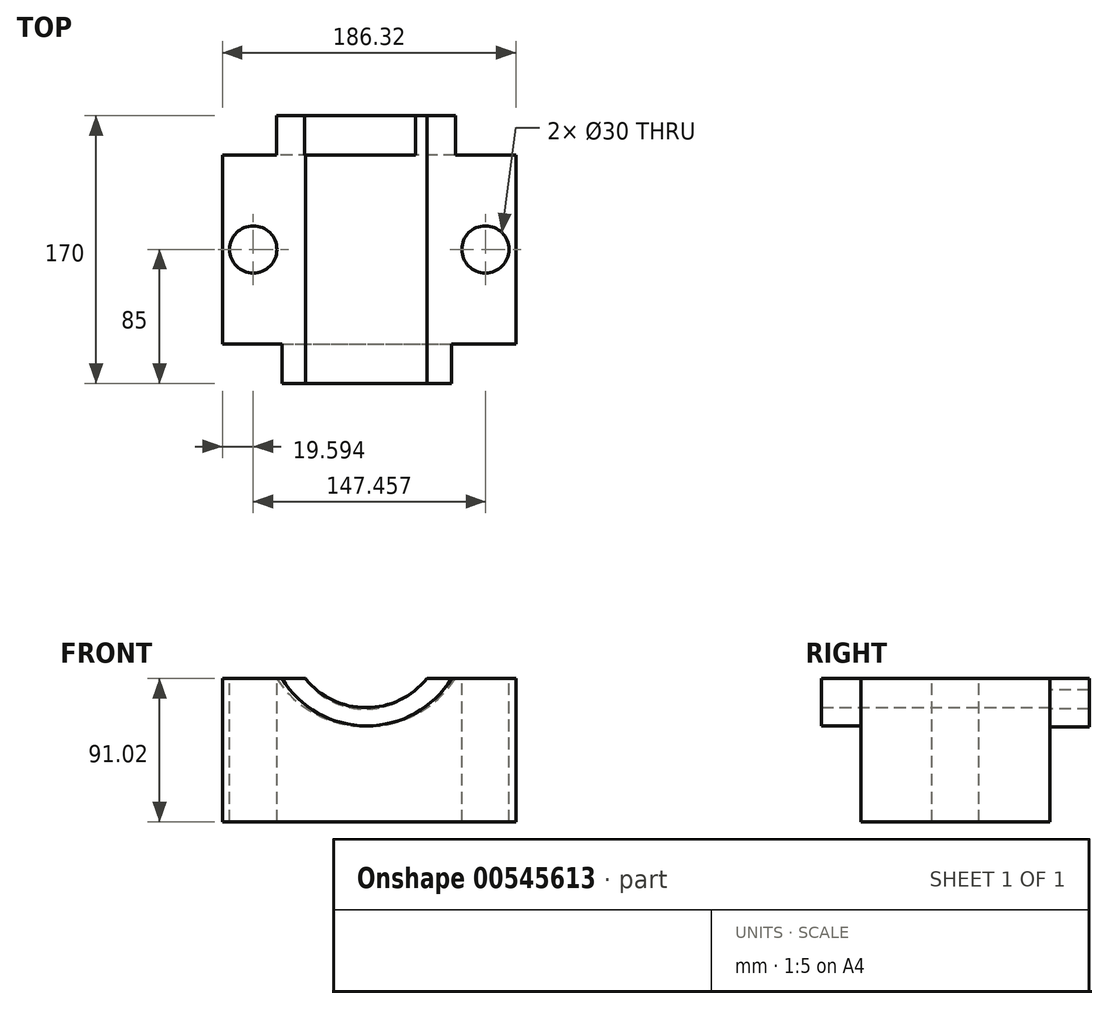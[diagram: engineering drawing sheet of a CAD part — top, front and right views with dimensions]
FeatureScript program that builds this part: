
annotation { "Feature Type Name" : "Feature", "Feature Type Description" : "" }
export const myFeature = defineFeature(function(context is Context, id is Id, definition is map)
    precondition{}
    {
        {
            var Q0;
            Q0=qCreatedBy(makeId("Front.planeOp"),FACE);
            var sketch = newSketch(context, id + "F0", { "sketchPlane" : qUnion([Q0])});
            skLineSegment(sketch, "E0.bottom", {"start": v(-92.59, 41.23) * mm, "end": v(93.73, 41.23) * mm});
            skLineSegment(sketch, "E0.top", {"start": v(-92.59, -49.79) * mm, "end": v(93.73, -49.79) * mm});
            skLineSegment(sketch, "E0.left", {"start": v(-92.59, 41.23) * mm, "end": v(-92.59, -49.79) * mm});
            skLineSegment(sketch, "E0.right", {"start": v(93.73, 41.23) * mm, "end": v(93.73, -49.79) * mm});
            skSolve(sketch);
        }
        {
            var Q0;
            Q0=makeQuery(id+"F0.imprint","IMPRINT",FACE,{"disambiguationData":[TD([[makeQuery(id+"F0.imprint","IMPRINT",EDGE,{"derivedFrom":sQuery(id+"F0.wireOp",EDGE,"E0.bottom")}),-1.0]])]});
            extrude(context, id + "F1", {"entities" : qUnion([Q0]), "depth" : 120 * mm, "offsetDistance" : 25 * mm, "symmetric" : true});
        }
        {
            var Q0;
            Q0=makeQuery(id+"F1.opExtrude","CAP_FACE",FACE,{"disambiguationData":[OSD([sQuery(id+"F0.wireOp",EDGE,"E0.bottom"),sQuery(id+"F0.wireOp",EDGE,"E0.top"),sQuery(id+"F0.wireOp",EDGE,"E0.left"),sQuery(id+"F0.wireOp",EDGE,"E0.right")])],"isStart":false});
            var sketch = newSketch(context, id + "F2", { "sketchPlane" : qUnion([Q0])});
            skArc(sketch, "E1", {"start": v(-40.37, 41.8) * mm, "mid": v(-1.7, 22.73) * mm, "end": v(37.24, 41.23) * mm});
            skArc(sketch, "E2", {"start": v(-55.21, 41.8) * mm, "mid": v(-1, 11.12) * mm, "end": v(53.21, 41.8) * mm});
            skSolve(sketch);
        }
        {
            var Q0;
            {var subQ0=sQuery(id+"F2.wireOp",EDGE,"E1");var subQ1=makeQuery(id+"F1.opExtrude","CAP_EDGE",EDGE,{"disambiguationData":[OSD([sQuery(id+"F0.wireOp",EDGE,"E0.bottom")])],"isStart":false});var subQ2=makeQuery(id+"F2.imprint","INTERSECT",VERTEX,{"disambiguationData":[OD(0.0)],"derivedFrom":[subQ1,subQ0]});Q0=makeQuery(id+"F2.imprint","IMPRINT",FACE,{"disambiguationData":[TD([[makeQuery(id+"F2.imprint","IMPRINT",EDGE,{"disambiguationData":[TD([[subQ2,1.0]])],"derivedFrom":subQ0}),-1.0]])]});}
            extrude(context, id + "F3", {"entities" : qUnion([Q0]), "operationType" : NewBodyOperationType.ADD, "depth" : 25 * mm, "offsetDistance" : 25 * mm});
        }
        {
            var Q0;
            Q0=makeQuery(id+"F1.opExtrude","CAP_FACE",FACE,{"disambiguationData":[OSD([sQuery(id+"F0.wireOp",EDGE,"E0.bottom"),sQuery(id+"F0.wireOp",EDGE,"E0.top"),sQuery(id+"F0.wireOp",EDGE,"E0.left"),sQuery(id+"F0.wireOp",EDGE,"E0.right")])],"isStart":true});
            var sketch = newSketch(context, id + "F4", { "sketchPlane" : qUnion([Q0])});
            skArc(sketch, "E3", {"start": v(-55.4, 41.23) * mm, "mid": v(1.44, 10.6) * mm, "end": v(58.3, 41.23) * mm});
            skArc(sketch, "E4", {"start": v(-36.65, 41.23) * mm, "mid": v(1.87, 21.76) * mm, "end": v(40.38, 41.23) * mm});
            skSolve(sketch);
        }
        {
            var Q0;
            {var subQ0=sQuery(id+"F4.wireOp",EDGE,"E3");Q0=makeQuery(id+"F4.imprint","IMPRINT",FACE,{"disambiguationData":[TD([[makeQuery(id+"F4.imprint","IMPRINT",EDGE,{"derivedFrom":subQ0}),1.0]])]});}
            extrude(context, id + "F5", {"entities" : qUnion([Q0]), "operationType" : NewBodyOperationType.ADD, "depth" : 25 * mm, "offsetDistance" : 25 * mm});
        }
        {
            var Q0;
            {var subQ0=sQuery(id+"F4.wireOp",EDGE,"E3");var subQ1=sQuery(id+"F0.wireOp",EDGE,"E0.bottom");var subQ2=makeQuery(id+"F1.opExtrude","CAP_EDGE",EDGE,{"disambiguationData":[OSD([subQ1])],"isStart":true});var subQ4=sQuery(id+"F2.wireOp",EDGE,"E1");var subQ5=makeQuery(id+"F1.opExtrude","CAP_EDGE",EDGE,{"disambiguationData":[OSD([subQ1])],"isStart":false});Q0=makeQuery(id+"F5.boolean.opBoolean","MERGE",FACE,{"derivedFrom":[makeQuery(id+"F3.boolean.opBoolean","MERGE",FACE,{"derivedFrom":[makeQuery(id+"F1.opExtrude","SWEPT_FACE",FACE,{"disambiguationData":[OSD([subQ1])]}),makeQuery(id+"F3.opExtrude","SWEPT_FACE",FACE,{"disambiguationData":[OSD([subQ1]),TDD([makeQuery(id+"F2.imprint","IMPRINT",EDGE,{"disambiguationData":[TD([[makeQuery(id+"F2.imprint","INTERSECT",VERTEX,{"disambiguationData":[OD(1.0)],"derivedFrom":[subQ5,subQ4]}),1.0]])],"derivedFrom":subQ5})])]}),makeQuery(id+"F3.opExtrude","SWEPT_FACE",FACE,{"disambiguationData":[OSD([subQ1]),TDD([makeQuery(id+"F2.imprint","IMPRINT",EDGE,{"disambiguationData":[TD([[makeQuery(id+"F2.imprint","INTERSECT",VERTEX,{"disambiguationData":[OD(0.0)],"derivedFrom":[subQ5,subQ4]}),-1.0]])],"derivedFrom":subQ5})])]})]}),makeQuery(id+"F5.opExtrude","SWEPT_FACE",FACE,{"disambiguationData":[OSD([subQ1]),TDD([makeQuery(id+"F4.imprint","IMPRINT",EDGE,{"disambiguationData":[TD([[makeQuery(id+"F4.imprint","INTERSECT",VERTEX,{"disambiguationData":[OD(0.0)],"derivedFrom":[subQ2,subQ0]}),1.0]])],"derivedFrom":subQ2})])]}),makeQuery(id+"F5.opExtrude","SWEPT_FACE",FACE,{"disambiguationData":[OSD([subQ1]),TDD([makeQuery(id+"F4.imprint","IMPRINT",EDGE,{"disambiguationData":[TD([[makeQuery(id+"F4.imprint","INTERSECT",VERTEX,{"disambiguationData":[OD(1.0)],"derivedFrom":[subQ2,subQ0]}),-1.0]])],"derivedFrom":subQ2})])]})]});}
            var sketch = newSketch(context, id + "F6", { "sketchPlane" : qUnion([Q0])});
            skLineSegment(sketch, "E5", {"start": v(-40.34, 60.63) * mm, "end": v(-40.34, -60.3) * mm});
            skLineSegment(sketch, "E6", {"start": v(-40.34, -60.3) * mm, "end": v(37.27, -60.3) * mm});
            skLineSegment(sketch, "E7", {"start": v(37.27, -60.3) * mm, "end": v(37.27, 60.3) * mm});
            skLineSegment(sketch, "E8", {"start": v(37.27, 60.3) * mm, "end": v(-40.34, 60.63) * mm});
            skSolve(sketch);
        }
        {
            var Q0;
            {var subQ0=sQuery(id+"F0.wireOp",EDGE,"E0.bottom");var subQ1=sQuery(id+"F2.wireOp",EDGE,"E1");Q0=makeQuery(id+"F3.boolean.opBoolean","SPLIT",FACE,{"disambiguationData":[TD([makeQuery(id+"F3.opExtrude","SWEPT_FACE",FACE,{"disambiguationData":[OSD([subQ1])]})])],"derivedFrom":makeQuery(id+"F1.opExtrude","CAP_FACE",FACE,{"disambiguationData":[OSD([subQ0,sQuery(id+"F0.wireOp",EDGE,"E0.top"),sQuery(id+"F0.wireOp",EDGE,"E0.left"),sQuery(id+"F0.wireOp",EDGE,"E0.right")])],"isStart":false})});}
            extrude(context, id + "F7", {"entities" : qUnion([Q0]), "operationType" : NewBodyOperationType.REMOVE, "oppositeDirection" : true, "depth" : 181 * mm, "offsetDistance" : 25 * mm});
        }
        {
            var Q0;
            {var subQ1=sQuery(id+"F0.wireOp",EDGE,"E0.bottom");var subQ8=sQuery(id+"F0.wireOp",EDGE,"E0.left");Q0=makeQuery(id+"F6.imprint","IMPRINT",FACE,{"disambiguationData":[TD([[makeQuery(id+"F6.imprint","IMPRINT",EDGE,{"derivedFrom":makeQuery(id+"F1.opExtrude","SWEPT_EDGE",EDGE,{"disambiguationData":[OSD([subQ1,subQ8])]})}),-1.0]])]});}
            var sketch = newSketch(context, id + "F8", { "sketchPlane" : qUnion([Q0])});
            skCircle(sketch, "E9", {"center": v(-73, 0) * mm, "radius": 10.27 * mm});
            skSolve(sketch);
        }
        {
            var Q0;
            {var subQ21=sQuery(id+"F6.wireOp",EDGE,"E7");Q0=makeQuery(id+"F6.imprint","IMPRINT",FACE,{"disambiguationData":[TD([[makeQuery(id+"F6.imprint","IMPRINT",EDGE,{"derivedFrom":subQ21}),-1.0]])]});}
            var sketch = newSketch(context, id + "F9", { "sketchPlane" : qUnion([Q0])});
            skCircle(sketch, "E10", {"center": v(74.46, 0) * mm, "radius": 10.85 * mm});
            skSolve(sketch);
        }
        {
            var Q0;
            Q0=sQuery(id+"F8.wireOp",VERTEX,"E9.center");
            var Q1;
            Q1=sQuery(id+"F9.wireOp",VERTEX,"E10.center");
            var Q2;
            Q2=makeQuery(id+"F1.opExtrude","SWEPT_BODY",BODY,{"disambiguationData":[OSD([sQuery(id+"F0.wireOp",EDGE,"E0.bottom"),sQuery(id+"F0.wireOp",EDGE,"E0.top"),sQuery(id+"F0.wireOp",EDGE,"E0.left"),sQuery(id+"F0.wireOp",EDGE,"E0.right")])]});
            hole(context, id + "F10", {"style" : HoleStyle.SIMPLE, "endStyle" : HoleEndStyle.THROUGH, "holeDiameter" : 30 * mm, "majorDiameter" : 5 * mm, "isTappedThrough" : true, "tappedDepth" : 12 * mm, "tapClearance" : 3, "locations" : qUnion([Q0, Q1]), "scope" : qUnion([Q2])});
        }
    });
